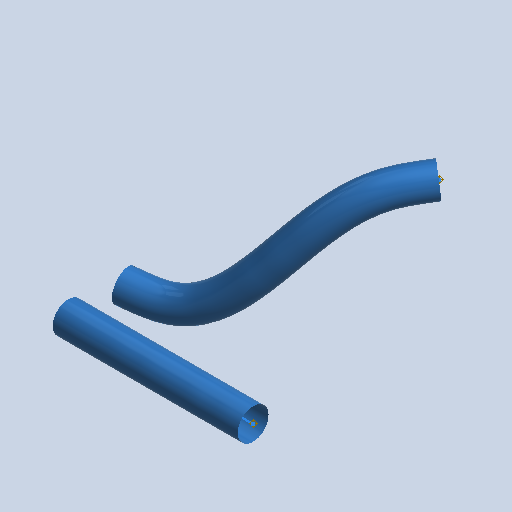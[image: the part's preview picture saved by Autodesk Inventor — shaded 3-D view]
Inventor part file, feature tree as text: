
AUTODESK INVENTOR PART (.ipt)
format: ipt  version: 2024 (Build 280153000, 153)  size: 199,168 bytes
history: native  units: mm (DEFAULTED — no unit token found)
features: other x10, plane x2, sketch x2, sweep x2
ambient origin geometry x8: Origin, YZ Plane, XZ Plane, XY Plane, X Axis, Y Axis, Z Axis, Center Point
bodies: Body1 (feature_tree), Body2 (feature_tree)
feature tree (16):
  other  "Work Point1"
  other  "Work Point2"
  other  "Wire1"
  plane  "Work Plane1"
  other  "Work Point3"
  other  "Work Point4"
  other  "Work Point7"
  other  "Work Point8"
  other  "Wire2"
  plane  "Work Plane3"
  sketch  "Sketch1"  dims[d0=0.0mm d1=0.0mm d4=0.0mm d5=0.0mm]
  other  "Srf1"
  sketch  "Sketch3"
  other  "Srf3"
  sweep  "SweepSrf1"
  sweep  "SweepSrf3"
